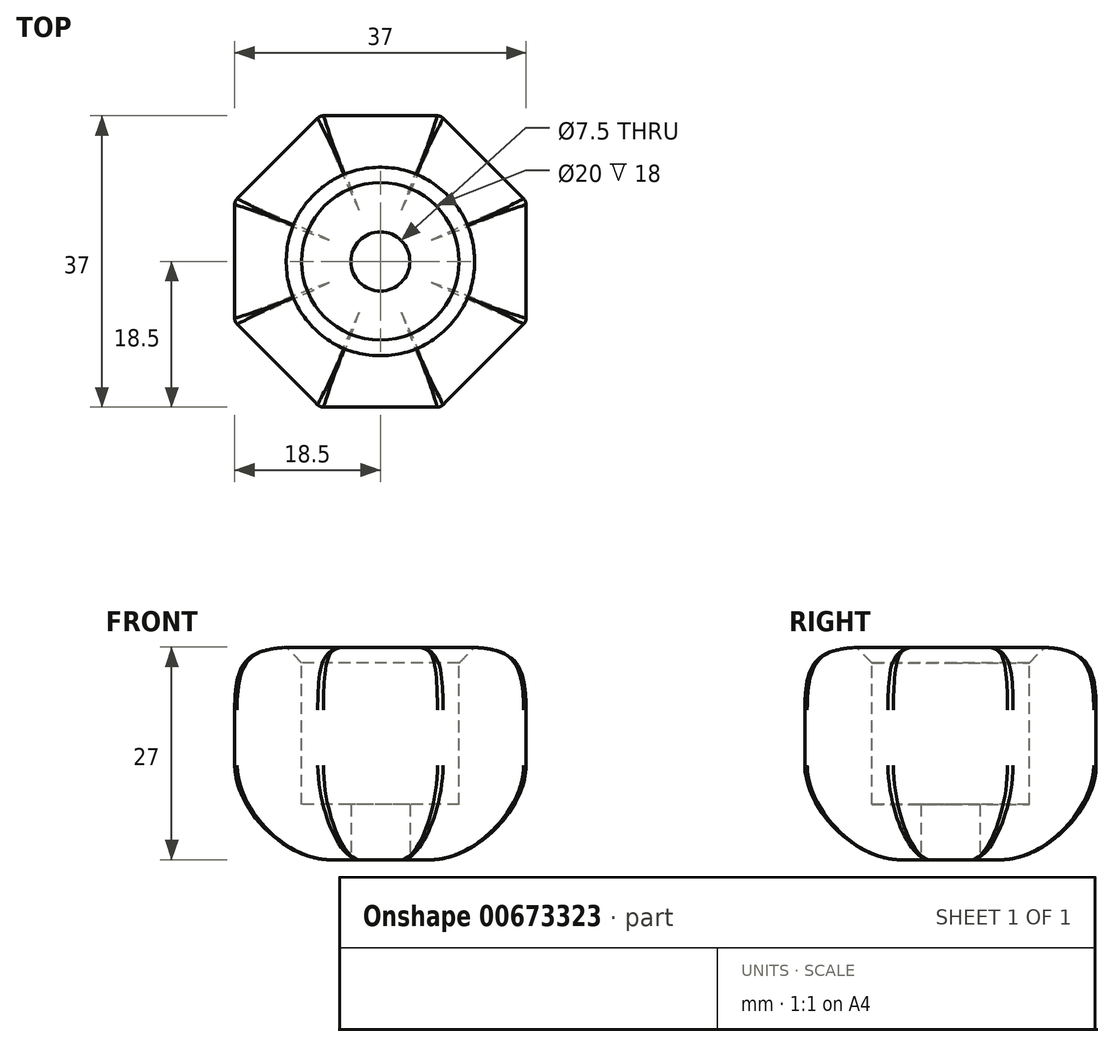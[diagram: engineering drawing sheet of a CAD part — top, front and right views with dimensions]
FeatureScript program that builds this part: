
annotation { "Feature Type Name" : "Feature", "Feature Type Description" : "" }
export const myFeature = defineFeature(function(context is Context, id is Id, definition is map)
    precondition{}
    {
        {
            var Q0;
            Q0=qCreatedBy(makeId("Top.planeOp"),FACE);
            var sketch = newSketch(context, id + "F0", { "sketchPlane" : qUnion([Q0])});
            skCircle(sketch, "E0.cCircle", {"center": v(0, 0) * mm, "radius": 18.5 * mm, "construction": true});
            skLineSegment(sketch, "E0.0", {"start": v(-7.66, 18.5) * mm, "end": v(7.66, 18.5) * mm});
            skLineSegment(sketch, "E0.1", {"start": v(7.66, 18.5) * mm, "end": v(18.5, 7.66) * mm});
            skLineSegment(sketch, "E0.2", {"start": v(18.5, 7.66) * mm, "end": v(18.5, -7.66) * mm});
            skLineSegment(sketch, "E0.3", {"start": v(18.5, -7.66) * mm, "end": v(7.66, -18.5) * mm});
            skLineSegment(sketch, "E0.4", {"start": v(7.66, -18.5) * mm, "end": v(-7.66, -18.5) * mm});
            skLineSegment(sketch, "E0.5", {"start": v(-7.66, -18.5) * mm, "end": v(-18.5, -7.66) * mm});
            skLineSegment(sketch, "E0.6", {"start": v(-18.5, -7.66) * mm, "end": v(-18.5, 7.66) * mm});
            skLineSegment(sketch, "E0.7", {"start": v(-18.5, 7.66) * mm, "end": v(-7.66, 18.5) * mm});
            skPoint(sketch, "E0.0.midPoint", {"position": v(0, 18.5) * mm});
            skCircle(sketch, "E1", {"center": v(0, 0) * mm, "radius": 3.75 * mm});
            skSolve(sketch);
        }
        {
            var Q0;
            Q0=qSketchRegion(id+"F0",true);
            extrude(context, id + "F1", {"entities" : qUnion([Q0]), "depth" : 27 * mm, "offsetDistance" : 25 * mm});
        }
        {
            var Q0;
            Q0=makeQuery(id+"F1.opExtrude","CAP_FACE",FACE,{"disambiguationData":[OSD([sQuery(id+"F0.wireOp",EDGE,"E0.0"),sQuery(id+"F0.wireOp",EDGE,"E0.1"),sQuery(id+"F0.wireOp",EDGE,"E0.2"),sQuery(id+"F0.wireOp",EDGE,"E0.3"),sQuery(id+"F0.wireOp",EDGE,"E0.4"),sQuery(id+"F0.wireOp",EDGE,"E0.5"),sQuery(id+"F0.wireOp",EDGE,"E0.6"),sQuery(id+"F0.wireOp",EDGE,"E0.7"),sQuery(id+"F0.wireOp",EDGE,"E1")])],"isStart":false});
            var sketch = newSketch(context, id + "F2", { "sketchPlane" : qUnion([Q0])});
            skCircle(sketch, "E2", {"center": v(0, 0) * mm, "radius": 10 * mm});
            skSolve(sketch);
        }
        {
            var Q0;
            Q0=qSketchRegion(id+"F2",true);
            extrude(context, id + "F3", {"entities" : qUnion([Q0]), "operationType" : NewBodyOperationType.REMOVE, "flatOperationType" : FlatOperationType.REMOVE, "oppositeDirection" : true, "depth" : 20 * mm, "offsetDistance" : 25 * mm, "domain" : OperationDomain.MODEL});
        }
        {
            var Q0;
            Q0=makeQuery(id+"F1.opExtrude","CAP_EDGE",EDGE,{"disambiguationData":[OSD([sQuery(id+"F0.wireOp",EDGE,"E0.0")])],"isStart":false});
            var Q1;
            Q1=makeQuery(id+"F1.opExtrude","CAP_EDGE",EDGE,{"disambiguationData":[OSD([sQuery(id+"F0.wireOp",EDGE,"E0.7")])],"isStart":false});
            var Q2;
            Q2=makeQuery(id+"F1.opExtrude","CAP_EDGE",EDGE,{"disambiguationData":[OSD([sQuery(id+"F0.wireOp",EDGE,"E0.6")])],"isStart":false});
            var Q3;
            Q3=makeQuery(id+"F1.opExtrude","CAP_EDGE",EDGE,{"disambiguationData":[OSD([sQuery(id+"F0.wireOp",EDGE,"E0.5")])],"isStart":false});
            var Q4;
            Q4=makeQuery(id+"F1.opExtrude","CAP_EDGE",EDGE,{"disambiguationData":[OSD([sQuery(id+"F0.wireOp",EDGE,"E0.4")])],"isStart":false});
            var Q5;
            Q5=makeQuery(id+"F1.opExtrude","CAP_EDGE",EDGE,{"disambiguationData":[OSD([sQuery(id+"F0.wireOp",EDGE,"E0.3")])],"isStart":false});
            var Q6;
            Q6=makeQuery(id+"F1.opExtrude","CAP_EDGE",EDGE,{"disambiguationData":[OSD([sQuery(id+"F0.wireOp",EDGE,"E0.2")])],"isStart":false});
            var Q7;
            Q7=makeQuery(id+"F1.opExtrude","CAP_EDGE",EDGE,{"disambiguationData":[OSD([sQuery(id+"F0.wireOp",EDGE,"E0.1")])],"isStart":false});
            fillet(context, id + "F4", {"entities" : qUnion([Q0, Q1, Q2, Q3, Q4, Q5, Q6, Q7]), "radius" : 8 * mm, "tangentPropagation" : true, "rho" : 0.6, "crossSection" : FilletCrossSection.CONIC, "allowEdgeOverflow" : false});
        }
        {
            var Q0;
            Q0=makeQuery(id+"F1.opExtrude","CAP_EDGE",EDGE,{"disambiguationData":[OSD([sQuery(id+"F0.wireOp",EDGE,"E0.1")])],"isStart":true});
            var Q1;
            Q1=makeQuery(id+"F1.opExtrude","CAP_EDGE",EDGE,{"disambiguationData":[OSD([sQuery(id+"F0.wireOp",EDGE,"E0.3")])],"isStart":true});
            var Q2;
            Q2=makeQuery(id+"F1.opExtrude","CAP_EDGE",EDGE,{"disambiguationData":[OSD([sQuery(id+"F0.wireOp",EDGE,"E0.5")])],"isStart":true});
            var Q3;
            Q3=makeQuery(id+"F1.opExtrude","CAP_EDGE",EDGE,{"disambiguationData":[OSD([sQuery(id+"F0.wireOp",EDGE,"E0.7")])],"isStart":true});
            var Q4;
            Q4=makeQuery(id+"F1.opExtrude","CAP_EDGE",EDGE,{"disambiguationData":[OSD([sQuery(id+"F0.wireOp",EDGE,"E0.2")])],"isStart":true});
            var Q5;
            Q5=makeQuery(id+"F1.opExtrude","CAP_EDGE",EDGE,{"disambiguationData":[OSD([sQuery(id+"F0.wireOp",EDGE,"E0.0")])],"isStart":true});
            var Q6;
            Q6=makeQuery(id+"F1.opExtrude","CAP_EDGE",EDGE,{"disambiguationData":[OSD([sQuery(id+"F0.wireOp",EDGE,"E0.6")])],"isStart":true});
            var Q7;
            Q7=makeQuery(id+"F1.opExtrude","CAP_EDGE",EDGE,{"disambiguationData":[OSD([sQuery(id+"F0.wireOp",EDGE,"E0.4")])],"isStart":true});
            fillet(context, id + "F5", {"entities" : qUnion([Q0, Q1, Q2, Q3, Q4, Q5, Q6, Q7]), "radius" : 12 * mm, "tangentPropagation" : true, "rho" : 0.35, "defaultsChanged" : true, "vertexSettings" : [], "crossSection" : FilletCrossSection.CONIC, "allowEdgeOverflow" : false});
        }
        {
            var Q0;
            Q0=makeQuery(id+"F1.opExtrude","CAP_FACE",FACE,{"disambiguationData":[OSD([sQuery(id+"F0.wireOp",EDGE,"E0.0"),sQuery(id+"F0.wireOp",EDGE,"E0.1"),sQuery(id+"F0.wireOp",EDGE,"E0.2"),sQuery(id+"F0.wireOp",EDGE,"E0.3"),sQuery(id+"F0.wireOp",EDGE,"E0.4"),sQuery(id+"F0.wireOp",EDGE,"E0.5"),sQuery(id+"F0.wireOp",EDGE,"E0.6"),sQuery(id+"F0.wireOp",EDGE,"E0.7"),sQuery(id+"F0.wireOp",EDGE,"E1")])],"isStart":false});
            chamfer(context, id + "F6", {"entities" : qUnion([Q0]), "width" : 2 * mm, "tangentPropagation" : true});
        }
        {
            var Q0;
            Q0=makeQuery(id+"F1.opExtrude","SWEPT_FACE",FACE,{"disambiguationData":[OSD([sQuery(id+"F0.wireOp",EDGE,"E0.0")])]});
            var Q1;
            Q1=makeQuery(id+"F1.opExtrude","SWEPT_FACE",FACE,{"disambiguationData":[OSD([sQuery(id+"F0.wireOp",EDGE,"E0.6")])]});
            var Q2;
            Q2=makeQuery(id+"F1.opExtrude","SWEPT_FACE",FACE,{"disambiguationData":[OSD([sQuery(id+"F0.wireOp",EDGE,"E0.4")])]});
            var Q3;
            Q3=makeQuery(id+"F1.opExtrude","SWEPT_FACE",FACE,{"disambiguationData":[OSD([sQuery(id+"F0.wireOp",EDGE,"E0.2")])]});
            fillet(context, id + "F7", {"entities" : qUnion([Q0, Q1, Q2, Q3]), "radius" : 1 * mm, "tangentPropagation" : true, "allowEdgeOverflow" : false});
        }
    });
